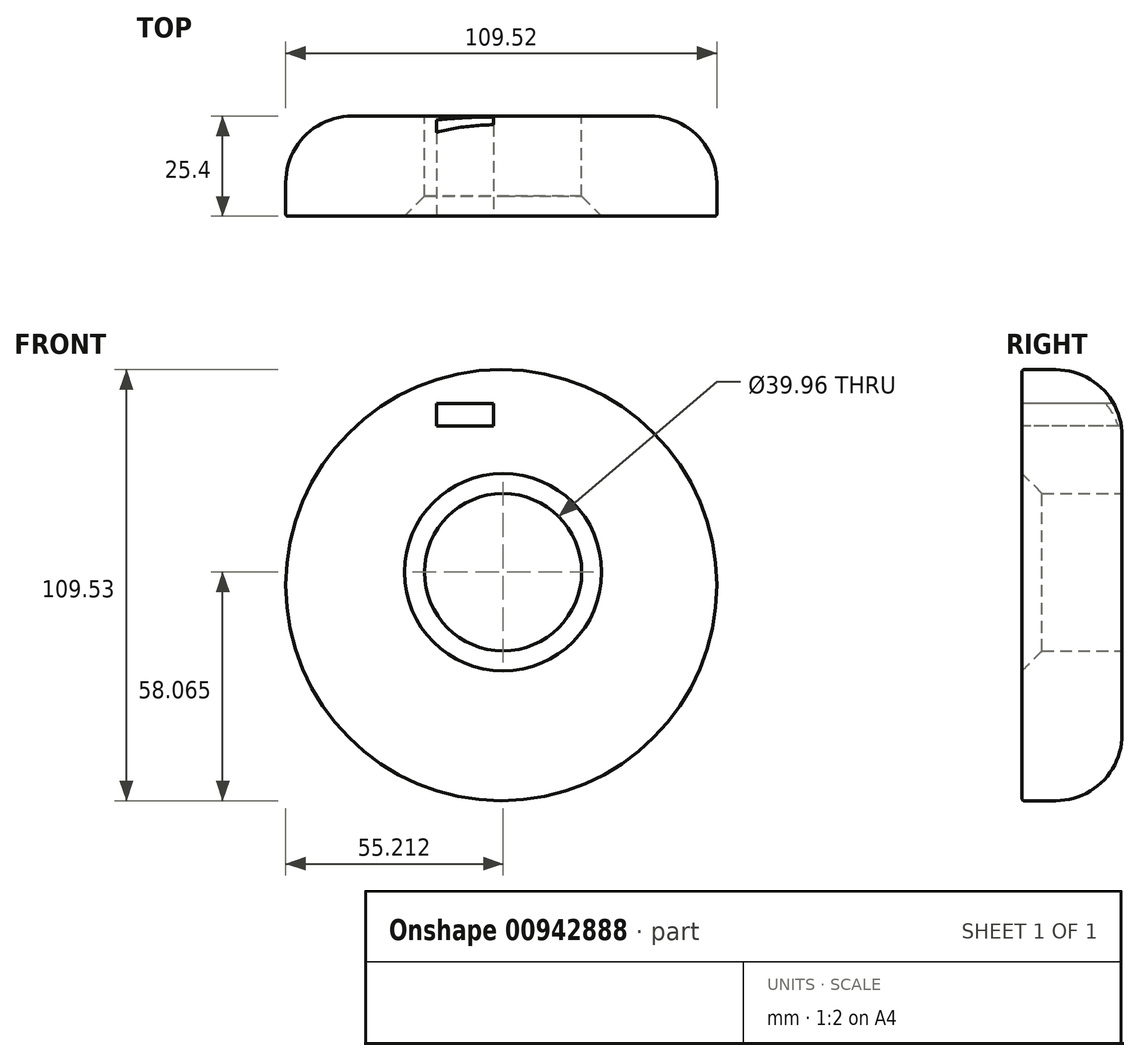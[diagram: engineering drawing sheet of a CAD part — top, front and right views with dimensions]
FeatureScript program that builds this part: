
annotation { "Feature Type Name" : "Feature", "Feature Type Description" : "" }
export const myFeature = defineFeature(function(context is Context, id is Id, definition is map)
    precondition{}
    {
        {
            var Q0;
            Q0=qCreatedBy(makeId("Front.planeOp"),FACE);
            var sketch = newSketch(context, id + "F0", { "sketchPlane" : qUnion([Q0])});
            skCircle(sketch, "E0", {"center": v(-1.21, -0.52) * mm, "radius": 54.76 * mm});
            skCircle(sketch, "E1", {"center": v(-0.76, 2.78) * mm, "radius": 19.98 * mm});
            skSolve(sketch);
        }
        {
            var Q0;
            Q0=makeQuery(id+"F0.imprint","IMPRINT",FACE,{"disambiguationData":[TD([[makeQuery(id+"F0.imprint","IMPRINT",EDGE,{"derivedFrom":sQuery(id+"F0.wireOp",EDGE,"E0")}),1.0]])]});
            extrude(context, id + "F1", {"entities" : qUnion([Q0]), "depth" : 25.4 * mm, "offsetDistance" : 25.4 * mm});
        }
        {
            var Q0;
            Q0=makeQuery(id+"F1.opExtrude","CAP_FACE",FACE,{"disambiguationData":[OSD([sQuery(id+"F0.wireOp",EDGE,"E0"),sQuery(id+"F0.wireOp",EDGE,"E1")])],"isStart":false});
            var sketch = newSketch(context, id + "F2", { "sketchPlane" : qUnion([Q0])});
            skLineSegment(sketch, "E2.bottom", {"start": v(-27.71, 47.4) * mm, "end": v(-28.61, 47.4) * mm});
            skLineSegment(sketch, "E2.top", {"start": v(-27.71, 27.24) * mm, "end": v(-28.61, 27.24) * mm});
            skLineSegment(sketch, "E2.left", {"start": v(-27.71, 47.4) * mm, "end": v(-27.71, 27.24) * mm});
            skLineSegment(sketch, "E2.right", {"start": v(-28.61, 47.4) * mm, "end": v(-28.61, 27.24) * mm});
            skLineSegment(sketch, "E3.bottom", {"start": v(-3.17, 45.61) * mm, "end": v(-17.65, 45.61) * mm});
            skLineSegment(sketch, "E3.top", {"start": v(-3.17, 39.9) * mm, "end": v(-17.65, 39.9) * mm});
            skLineSegment(sketch, "E3.left", {"start": v(-3.17, 45.61) * mm, "end": v(-3.17, 39.9) * mm});
            skLineSegment(sketch, "E3.right", {"start": v(-17.65, 45.61) * mm, "end": v(-17.65, 39.9) * mm});
            skSolve(sketch);
        }
        {
            var Q0;
            Q0=makeQuery(id+"F2.imprint","IMPRINT",FACE,{"disambiguationData":[TD([[makeQuery(id+"F2.imprint","IMPRINT",EDGE,{"derivedFrom":sQuery(id+"F2.wireOp",EDGE,"E3.bottom")}),1.0]])]});
            extrude(context, id + "F3", {"entities" : qUnion([Q0]), "operationType" : NewBodyOperationType.REMOVE, "oppositeDirection" : true, "depth" : 25.4 * mm, "offsetDistance" : 25.4 * mm});
        }
        {
            var Q0;
            Q0=makeQuery(id+"F1.opExtrude","CAP_EDGE",EDGE,{"disambiguationData":[OSD([sQuery(id+"F0.wireOp",EDGE,"E0")])],"isStart":false});
            fillet(context, id + "F4", {"entities" : qUnion([Q0]), "radius" : 0.5 * mm, "tangentPropagation" : true, "allowEdgeOverflow" : false});
        }
        {
            var Q0;
            Q0=makeQuery(id+"F1.opExtrude","CAP_EDGE",EDGE,{"disambiguationData":[OSD([sQuery(id+"F0.wireOp",EDGE,"E1")])],"isStart":false});
            chamfer(context, id + "F5", {"entities" : qUnion([Q0]), "width" : 5.08 * mm, "tangentPropagation" : true});
        }
        {
            var Q0;
            Q0=makeQuery(id+"F1.opExtrude","CAP_EDGE",EDGE,{"disambiguationData":[OSD([sQuery(id+"F0.wireOp",EDGE,"E0")])],"isStart":true});
            fillet(context, id + "F6", {"entities" : qUnion([Q0]), "radius" : 16.87 * mm, "tangentPropagation" : true, "allowEdgeOverflow" : false});
        }
    });
